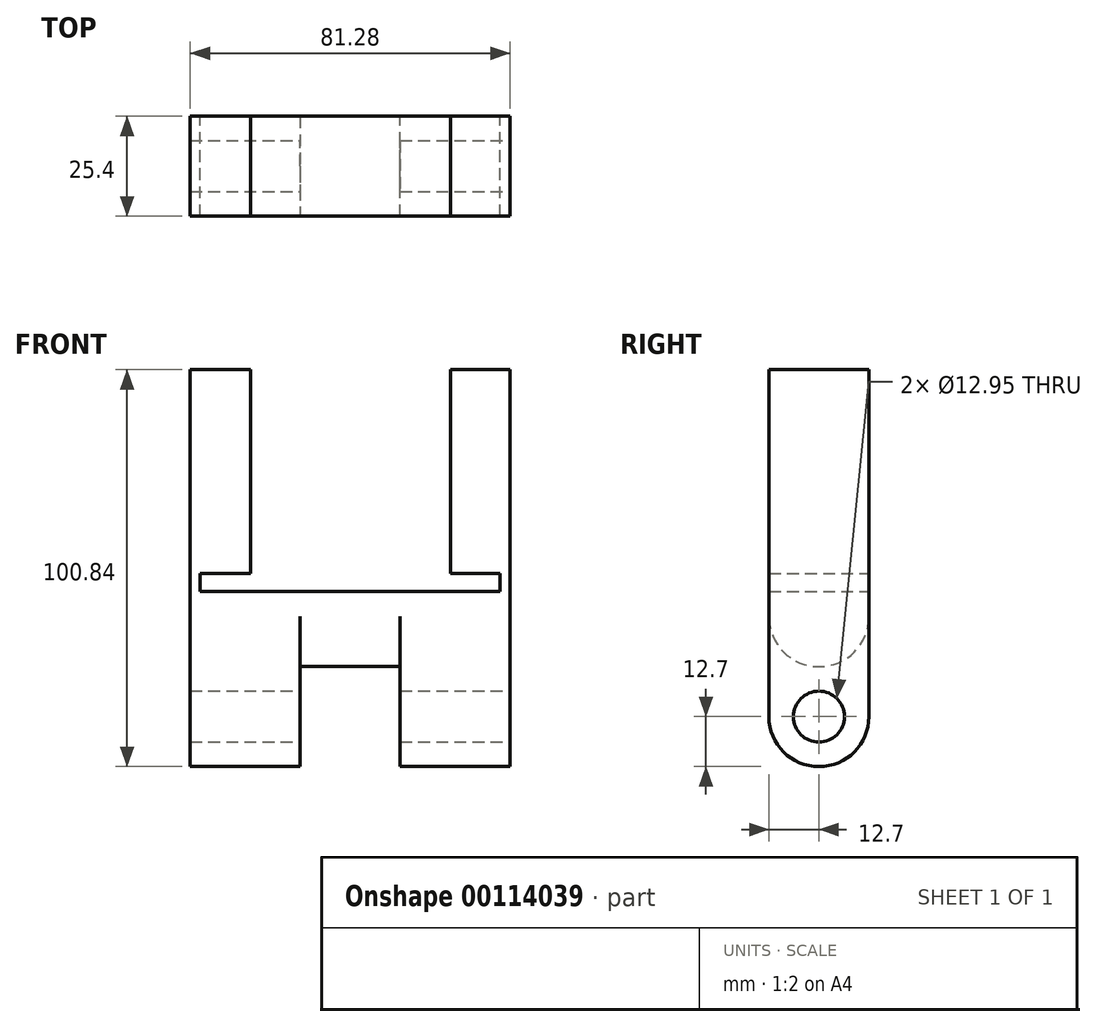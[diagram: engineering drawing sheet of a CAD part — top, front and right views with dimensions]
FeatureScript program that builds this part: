
annotation { "Feature Type Name" : "Feature", "Feature Type Description" : "" }
export const myFeature = defineFeature(function(context is Context, id is Id, definition is map)
    precondition{}
    {
        {
            var Q0;
            Q0=qCreatedBy(makeId("Front.planeOp"),FACE);
            var sketch = newSketch(context, id + "F0", { "sketchPlane" : qUnion([Q0])});
            skLineSegment(sketch, "E0", {"start": v(-12.7, 0) * mm, "end": v(-12.7, 25.4) * mm});
            skLineSegment(sketch, "E1", {"start": v(-12.7, 25.4) * mm, "end": v(12.7, 25.4) * mm});
            skLineSegment(sketch, "E2", {"start": v(12.7, 25.4) * mm, "end": v(12.7, 0) * mm});
            skLineSegment(sketch, "E3", {"start": v(12.7, 0) * mm, "end": v(40.64, 0) * mm});
            skLineSegment(sketch, "E4", {"start": v(40.64, 0) * mm, "end": v(40.64, 44.45) * mm});
            skLineSegment(sketch, "E5", {"start": v(40.64, 44.45) * mm, "end": v(-40.64, 44.45) * mm});
            skLineSegment(sketch, "E6", {"start": v(-40.64, 44.45) * mm, "end": v(-40.64, 0) * mm});
            skLineSegment(sketch, "E7", {"start": v(-40.64, 0) * mm, "end": v(-12.7, 0) * mm});
            skLineSegment(sketch, "E8", {"start": v(-38.1, 44.45) * mm, "end": v(-38.1, 49.11) * mm});
            skLineSegment(sketch, "E9", {"start": v(38.1, 44.45) * mm, "end": v(38.1, 49.11) * mm});
            skLineSegment(sketch, "E10", {"start": v(-38.1, 49.11) * mm, "end": v(-25.34, 49.11) * mm});
            skLineSegment(sketch, "E11", {"start": v(38.1, 49.11) * mm, "end": v(25.46, 49.11) * mm});
            skLineSegment(sketch, "E12", {"start": v(-38.1, 100.84) * mm, "end": v(38.1, 100.84) * mm});
            skLineSegment(sketch, "E13", {"start": v(25.46, 49.11) * mm, "end": v(25.46, 100.84) * mm});
            skLineSegment(sketch, "E14", {"start": v(-25.34, 49.11) * mm, "end": v(-25.34, 100.84) * mm});
            skLineSegment(sketch, "E15", {"start": v(-38.1, 100.84) * mm, "end": v(-40.64, 100.84) * mm});
            skLineSegment(sketch, "E16", {"start": v(-40.64, 100.84) * mm, "end": v(-40.64, 44.45) * mm});
            skLineSegment(sketch, "E17", {"start": v(40.64, 44.45) * mm, "end": v(40.64, 100.84) * mm});
            skLineSegment(sketch, "E18", {"start": v(40.64, 100.84) * mm, "end": v(38.1, 100.84) * mm});
            skSolve(sketch);
        }
        {
            var Q0;
            Q0=makeQuery(id+"F0.imprint","IMPRINT",FACE,{"disambiguationData":[TD([[makeQuery(id+"F0.imprint","IMPRINT",EDGE,{"derivedFrom":sQuery(id+"F0.wireOp",EDGE,"E0")}),1.0]])]});
            var Q1;
            {var subQ5=sQuery(id+"F0.wireOp",EDGE,"E8");Q1=makeQuery(id+"F0.imprint","IMPRINT",FACE,{"disambiguationData":[TD([[makeQuery(id+"F0.imprint","IMPRINT",EDGE,{"derivedFrom":subQ5}),1.0]])]});}
            var Q2;
            {var subQ5=sQuery(id+"F0.wireOp",EDGE,"E9");Q2=makeQuery(id+"F0.imprint","IMPRINT",FACE,{"disambiguationData":[TD([[makeQuery(id+"F0.imprint","IMPRINT",EDGE,{"derivedFrom":subQ5}),-1.0]])]});}
            extrude(context, id + "F1", {"entities" : qUnion([Q0, Q1, Q2]), "endBound" : BoundingType.SYMMETRIC, "depth" : 25.4 * mm});
        }
        {
            var Q0;
            Q0=qCreatedBy(makeId("Right.planeOp"),FACE);
            var sketch = newSketch(context, id + "F2", { "sketchPlane" : qUnion([Q0])});
            skArc(sketch, "E19", {"start": v(-12.7, 38.1) * mm, "mid": v(0, 25.4) * mm, "end": v(12.7, 38.1) * mm});
            skLineSegment(sketch, "E20", {"start": v(-12.7, 38.1) * mm, "end": v(-12.7, 24.45) * mm});
            skLineSegment(sketch, "E21", {"start": v(-12.7, 24.45) * mm, "end": v(12.7, 24.45) * mm});
            skLineSegment(sketch, "E22", {"start": v(12.7, 24.45) * mm, "end": v(12.7, 38.1) * mm});
            skSolve(sketch);
        }
        {
            var Q0;
            Q0 = qSketchRegion(id + "F2", true);
            extrude(context, id + "F3", {"entities" : qUnion([Q0]), "operationType" : NewBodyOperationType.REMOVE, "endBound" : BoundingType.SYMMETRIC, "depth" : 25.4 * mm});
        }
        {
            var Q0;
            Q0=makeQuery(id+"F1.opExtrude","SWEPT_FACE",FACE,{"disambiguationData":[OSD([sQuery(id+"F0.wireOp",EDGE,"E4")])]});
            var sketch = newSketch(context, id + "F4", { "sketchPlane" : qUnion([Q0])});
            skArc(sketch, "E23", {"start": v(-12.7, 12.7) * mm, "mid": v(0, 0) * mm, "end": v(12.7, 12.7) * mm});
            skPoint(sketch, "E23.centerSnap0", {"position": v(0, 0) * mm});
            skLineSegment(sketch, "E24", {"start": v(-12.7, 12.7) * mm, "end": v(-12.7, 0) * mm});
            skLineSegment(sketch, "E25", {"start": v(-12.7, 0) * mm, "end": v(12.7, 0) * mm});
            skLineSegment(sketch, "E26", {"start": v(12.7, 0) * mm, "end": v(12.7, 12.7) * mm});
            skCircle(sketch, "E27", {"center": v(0, 12.7) * mm, "radius": 6.48 * mm});
            skSolve(sketch);
        }
        {
            var Q0;
            Q0 = qSketchRegion(id + "F4", true);
            extrude(context, id + "F5", {"entities" : qUnion([Q0]), "operationType" : NewBodyOperationType.REMOVE, "endBound" : BoundingType.THROUGH_ALL, "oppositeDirection" : true, "depth" : 25.4 * mm});
        }
    });
